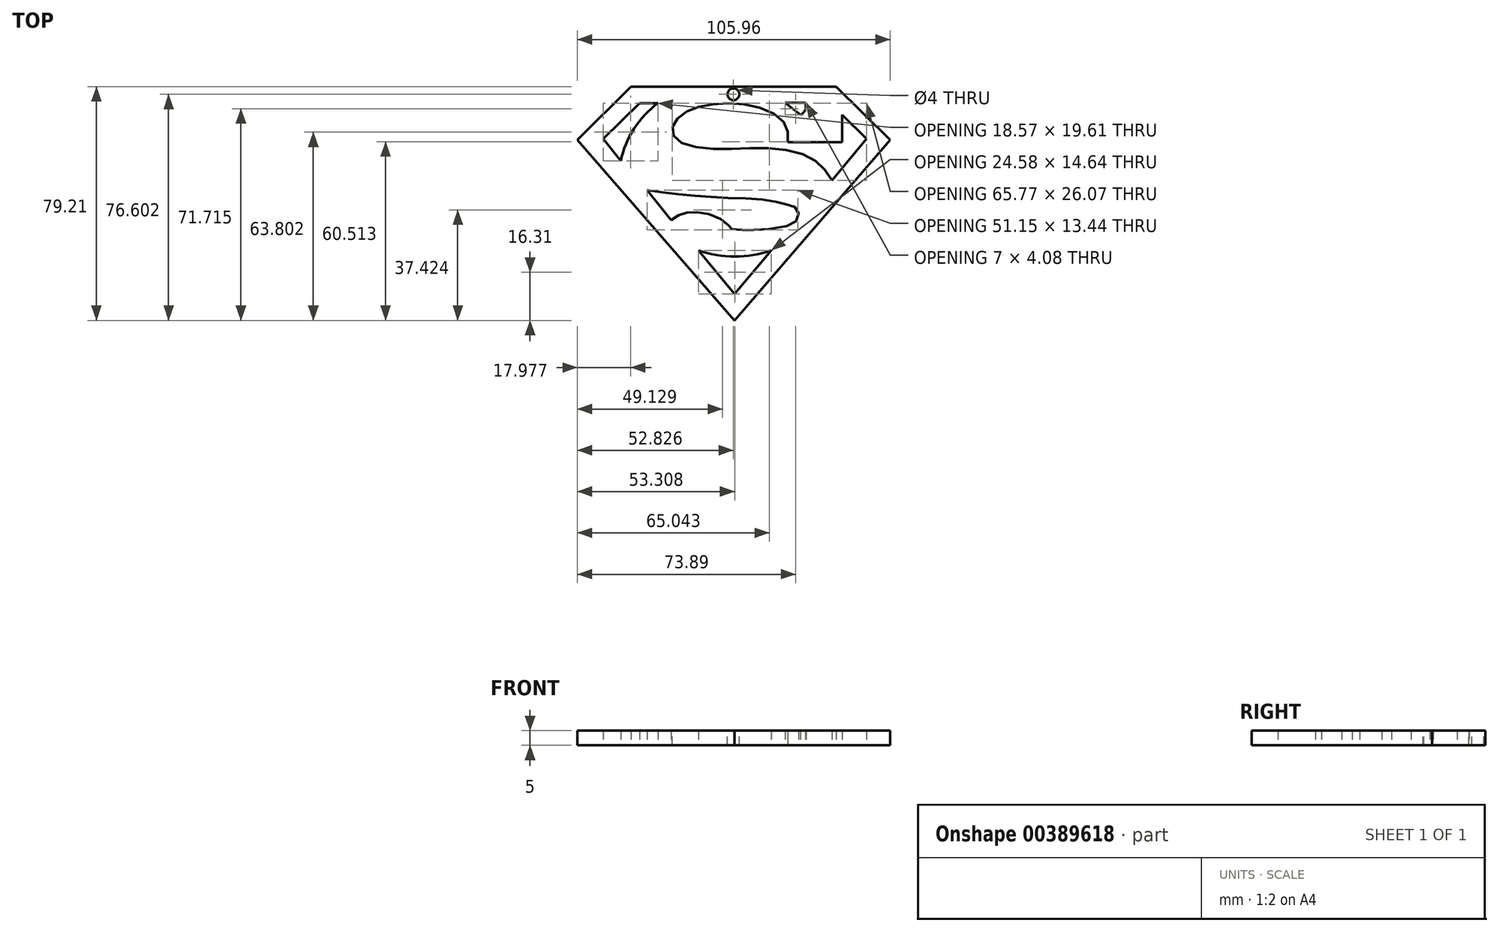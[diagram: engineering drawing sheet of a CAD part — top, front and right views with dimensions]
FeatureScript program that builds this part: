
annotation { "Feature Type Name" : "Feature", "Feature Type Description" : "" }
export const myFeature = defineFeature(function(context is Context, id is Id, definition is map)
    precondition{}
    {
        {
            var Q0;
            Q0=qCreatedBy(makeId("Top.planeOp"),FACE);
            var sketch = newSketch(context, id + "F0", { "sketchPlane" : qUnion([Q0])});
            skLineSegment(sketch, "E0", {"start": v(17.87, 32.01) * mm, "end": v(24.66, 32.01) * mm});
            skLineSegment(sketch, "E1", {"start": v(17.87, 32.01) * mm, "end": v(23.08, 27.94) * mm});
            skArc(sketch, "E2", {"start": v(23.08, 27.94) * mm, "mid": v(24.65, 29.67) * mm, "end": v(24.66, 32.01) * mm});
            skLineSegment(sketch, "E3", {"start": v(-25.26, 31.87) * mm, "end": v(-31.46, 31.87) * mm});
            skLineSegment(sketch, "E4", {"start": v(-31.46, 31.87) * mm, "end": v(-43.83, 19.76) * mm});
            skLineSegment(sketch, "E5", {"start": v(-43.83, 19.76) * mm, "end": v(-37.84, 12.25) * mm});
            skArc(sketch, "E6", {"start": v(-25.26, 31.87) * mm, "mid": v(-33.34, 23.2) * mm, "end": v(-37.84, 12.25) * mm});
            skLineSegment(sketch, "E7", {"start": v(-11.5, -18.11) * mm, "end": v(0.62, -32.75) * mm});
            skLineSegment(sketch, "E8", {"start": v(0.62, -32.75) * mm, "end": v(13.08, -18.11) * mm});
            skArc(sketch, "E9", {"start": v(-11.5, -18.11) * mm, "mid": v(0.79, -20.15) * mm, "end": v(13.08, -18.11) * mm});
            skFitSpline(sketch, "E10", {"points": [v(18.69, 18.64) * mm, v(17.86, 24.73) * mm, v(8.88, 30.4) * mm, v(-5.57, 31.65) * mm, v(-15.78, 28.86) * mm, v(-20.12, 24.21) * mm, v(-19.19, 19.78) * mm, v(-7.11, 16.37) * mm, v(12.19, 16.58) * mm, v(27.46, 12.76) * mm, v(33.76, 5.74) * mm], "startDerivative": vector(5.3, 82.87) * mm, "endDerivative": vector(53.92, -81.85) * mm});
            skLineSegment(sketch, "E11", {"start": v(33.76, 5.74) * mm, "end": v(45.41, 19.77) * mm});
            skLineSegment(sketch, "E12", {"start": v(45.41, 19.77) * mm, "end": v(37.08, 27.88) * mm});
            skLineSegment(sketch, "E13", {"start": v(37.08, 27.88) * mm, "end": v(37.08, 18.64) * mm});
            skFitSpline(sketch, "E14", {"points": [v(-28.96, 2.4) * mm, v(-15.86, 0.75) * mm, v(-1.51, -0.23) * mm, v(12.53, -1.1) * mm, v(19.03, -2.65) * mm, v(22.02, -4.15) * mm, v(21.97, -7.4) * mm, v(16.4, -10.29) * mm, v(-0.58, -10.7) * mm, v(-1.15, -9.88) * mm, v(-5.48, -6.57) * mm, v(-12.92, -5.13) * mm, v(-17.3, -5.75) * mm, v(-20.81, -7.7) * mm], "startDerivative": vector(122.53, -16.95) * mm, "endDerivative": vector(-58.36, -38.49) * mm});
            skLineSegment(sketch, "E15", {"start": v(-28.96, 2.4) * mm, "end": v(-20.81, -7.7) * mm});
            skLineSegment(sketch, "E16", {"start": v(-34.43, 37.47) * mm, "end": v(35.05, 37.47) * mm});
            skLineSegment(sketch, "E17", {"start": v(35.05, 37.47) * mm, "end": v(53.44, 19.37) * mm});
            skLineSegment(sketch, "E18", {"start": v(53.44, 19.37) * mm, "end": v(0.62, -41.74) * mm});
            skLineSegment(sketch, "E19", {"start": v(0.62, -41.74) * mm, "end": v(-52.52, 19.37) * mm});
            skLineSegment(sketch, "E20", {"start": v(-52.52, 19.37) * mm, "end": v(-34.43, 37.47) * mm});
            skLineSegment(sketch, "E21", {"start": v(37.08, 18.64) * mm, "end": v(18.69, 18.64) * mm});
            skSolve(sketch);
        }
        {
            var Q0;
            Q0 = qSketchRegion(id + "F0", true);
            extrude(context, id + "F1", {"entities" : qUnion([Q0]), "depth" : 5 * mm});
        }
        {
            var Q0;
            Q0=makeQuery(id+"F1.opExtrude","CAP_FACE",FACE,{"disambiguationData":[OSD([sQuery(id+"F0.wireOp",EDGE,"E0"),sQuery(id+"F0.wireOp",EDGE,"E1"),sQuery(id+"F0.wireOp",EDGE,"E2"),sQuery(id+"F0.wireOp",EDGE,"E3"),sQuery(id+"F0.wireOp",EDGE,"E4"),sQuery(id+"F0.wireOp",EDGE,"E5"),sQuery(id+"F0.wireOp",EDGE,"E6"),sQuery(id+"F0.wireOp",EDGE,"E7"),sQuery(id+"F0.wireOp",EDGE,"E8"),sQuery(id+"F0.wireOp",EDGE,"E9"),sQuery(id+"F0.wireOp",EDGE,"E10"),sQuery(id+"F0.wireOp",EDGE,"E11"),sQuery(id+"F0.wireOp",EDGE,"E12"),sQuery(id+"F0.wireOp",EDGE,"E13"),sQuery(id+"F0.wireOp",EDGE,"E14"),sQuery(id+"F0.wireOp",EDGE,"E15"),sQuery(id+"F0.wireOp",EDGE,"E16"),sQuery(id+"F0.wireOp",EDGE,"E17"),sQuery(id+"F0.wireOp",EDGE,"E18"),sQuery(id+"F0.wireOp",EDGE,"E19"),sQuery(id+"F0.wireOp",EDGE,"E20"),sQuery(id+"F0.wireOp",EDGE,"E21")])],"isStart":false});
            var sketch = newSketch(context, id + "F2", { "sketchPlane" : qUnion([Q0])});
            skCircle(sketch, "E22", {"center": v(0.3, 34.86) * mm, "radius": 2 * mm});
            skPoint(sketch, "E22.centerSnap0", {"position": v(0.3, 37.47) * mm});
            skSolve(sketch);
        }
        {
            var Q0;
            Q0 = qSketchRegion(id + "F2", true);
            var Q1;
            Q1=makeQuery(id+"F1.opExtrude","CAP_FACE",FACE,{"disambiguationData":[OSD([sQuery(id+"F0.wireOp",EDGE,"E0"),sQuery(id+"F0.wireOp",EDGE,"E1"),sQuery(id+"F0.wireOp",EDGE,"E2"),sQuery(id+"F0.wireOp",EDGE,"E3"),sQuery(id+"F0.wireOp",EDGE,"E4"),sQuery(id+"F0.wireOp",EDGE,"E5"),sQuery(id+"F0.wireOp",EDGE,"E6"),sQuery(id+"F0.wireOp",EDGE,"E7"),sQuery(id+"F0.wireOp",EDGE,"E8"),sQuery(id+"F0.wireOp",EDGE,"E9"),sQuery(id+"F0.wireOp",EDGE,"E10"),sQuery(id+"F0.wireOp",EDGE,"E11"),sQuery(id+"F0.wireOp",EDGE,"E12"),sQuery(id+"F0.wireOp",EDGE,"E13"),sQuery(id+"F0.wireOp",EDGE,"E14"),sQuery(id+"F0.wireOp",EDGE,"E15"),sQuery(id+"F0.wireOp",EDGE,"E16"),sQuery(id+"F0.wireOp",EDGE,"E17"),sQuery(id+"F0.wireOp",EDGE,"E18"),sQuery(id+"F0.wireOp",EDGE,"E19"),sQuery(id+"F0.wireOp",EDGE,"E20"),sQuery(id+"F0.wireOp",EDGE,"E21")])],"isStart":true});
            extrude(context, id + "F3", {"entities" : qUnion([Q0]), "operationType" : NewBodyOperationType.REMOVE, "endBound" : BoundingType.UP_TO_SURFACE, "oppositeDirection" : true, "endBoundEntityFace" : qUnion([Q1]), "depth" : 25 * mm});
        }
    });
